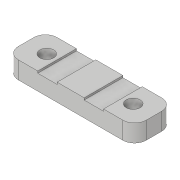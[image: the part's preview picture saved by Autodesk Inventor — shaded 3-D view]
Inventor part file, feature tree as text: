
AUTODESK INVENTOR PART (.ipt)
format: ipt  version: 2020 (Build 240168000, 168)  size: 269,824 bytes
history: native  units: in
note: dims shown in document units (in); Inventor stores cm internally (conversion verified against a paired STEP export)
features: extrude x5, sketch x5, mirror x2, plane x1, fillet x1
ambient origin geometry x8: Origin, YZ Plane, XZ Plane, XY Plane, X Axis, Y Axis, Z Axis, Center Point
bodies: Solid1 (feature_tree)
feature tree (14):
  extrude  "Extrusion1"  Depth=0.3937in
  extrude  "Extrusion2"  Depth=0.1575in TaperAngle=0.0deg
  plane  "Work Plane1"
  mirror  "Mirror1"
  fillet  "Fillet1"  [1 undecoded]
  extrude  "Extrusion3"  Depth=0.1417in
  extrude  "Extrusion4"  Depth=0.3937in
  mirror  "Mirror2"
  extrude  "Extrusion5"  Depth=0.315in
  sketch  "Sketch1"  dims[d0=1.2992in d1=0.3937in]
  sketch  "Sketch2"  dims[d2=0.1575in d3=0.0in d5=0.1575in d6=0.0in d7=-0.6496in]
  sketch  "Sketch3"  dims[d8=0.1181in d9=0.1417in]
  sketch  "Sketch4"  dims[d10=0.2756in d11=0.3937in]
  sketch  "Sketch5"  dims[d12=0.0197in d13=0.0in d14=0.315in d15=0.3937in d16=0.1181in d17=0.0197in d18=0.0in d19=0.0197in d20=0.0in]
note: 1 required parameter value undecoded (feature->parameter linkage not recoverable at this tier; creation-order binding heuristic only, values carry confidence <= 0.55)
